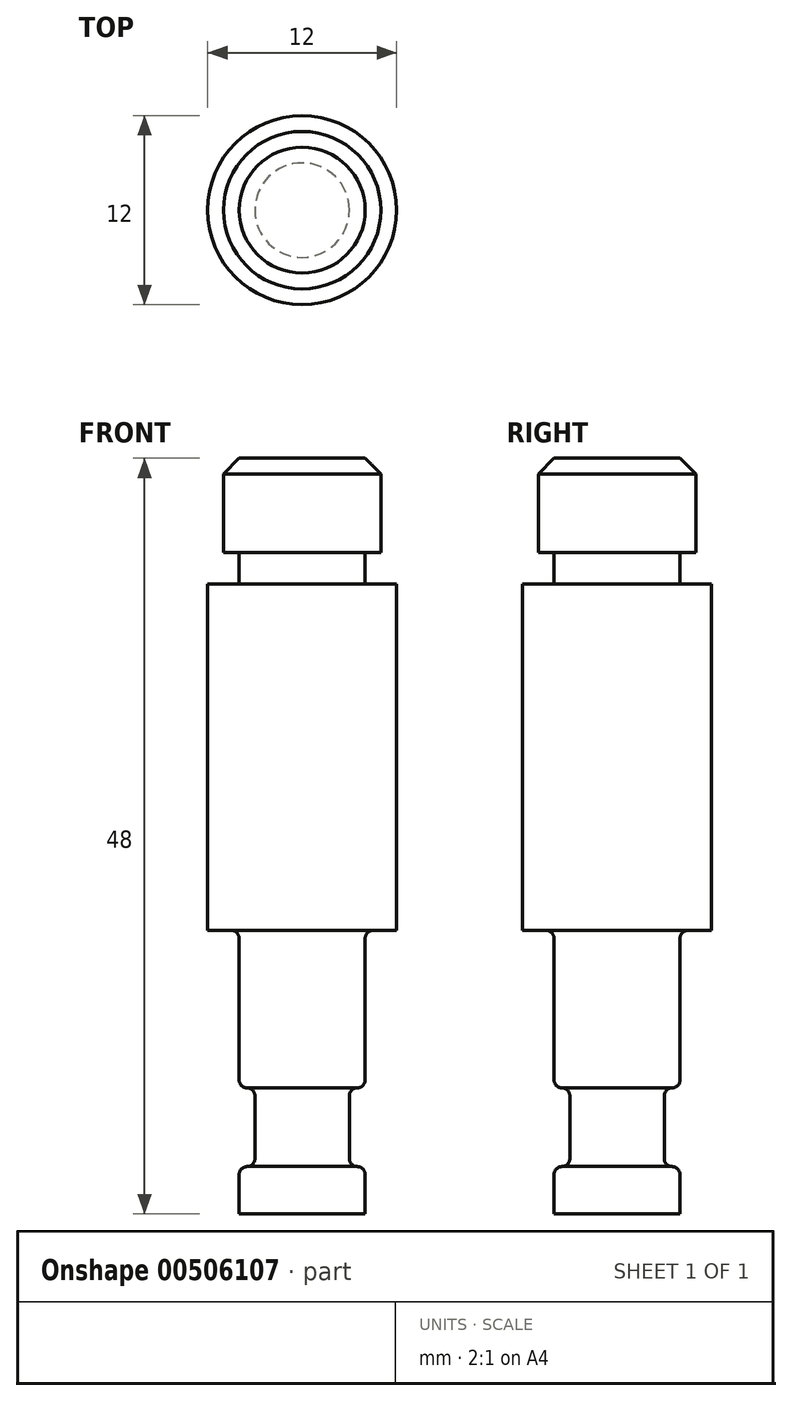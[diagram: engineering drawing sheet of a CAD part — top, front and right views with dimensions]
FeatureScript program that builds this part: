
annotation { "Feature Type Name" : "Feature", "Feature Type Description" : "" }
export const myFeature = defineFeature(function(context is Context, id is Id, definition is map)
    precondition{}
    {
        {
            var Q0;
            Q0=qCreatedBy(makeId("Top.planeOp"),FACE);
            var sketch = newSketch(context, id + "F0", { "sketchPlane" : qUnion([Q0])});
            skCircle(sketch, "E0", {"center": v(0, 0) * mm, "radius": 6 * mm});
            skSolve(sketch);
        }
        {
            var Q0;
            Q0=makeQuery(id+"F0.imprint","IMPRINT",FACE,{"disambiguationData":[TD([[makeQuery(id+"F0.imprint","IMPRINT",EDGE,{"derivedFrom":sQuery(id+"F0.wireOp",EDGE,"E0")}),1.0]])]});
            extrude(context, id + "F1", {"entities" : qUnion([Q0]), "oppositeDirection" : true, "depth" : 40 * mm});
        }
        {
            var Q0;
            Q0=makeQuery(id+"F1.opExtrude","CAP_FACE",FACE,{"disambiguationData":[OSD([sQuery(id+"F0.wireOp",EDGE,"E0")])],"isStart":true});
            var sketch = newSketch(context, id + "F2", { "sketchPlane" : qUnion([Q0])});
            skCircle(sketch, "E1", {"center": v(0, 0) * mm, "radius": 5 * mm});
            skSolve(sketch);
        }
        {
            var Q0;
            Q0 = qSketchRegion(id + "F2", true);
            extrude(context, id + "F3", {"entities" : qUnion([Q0]), "operationType" : NewBodyOperationType.ADD, "depth" : 8 * mm});
        }
        {
            var Q0;
            Q0=qCreatedBy(makeId("Right.planeOp"),FACE);
            var sketch = newSketch(context, id + "F4", { "sketchPlane" : qUnion([Q0])});
            skLineSegment(sketch, "E2", {"start": v(0, -52.59) * mm, "end": v(0, 0) * mm, "construction": true});
            skLineSegment(sketch, "E3", {"start": v(6, 0) * mm, "end": v(6, -40) * mm});
            skLineSegment(sketch, "E4", {"start": v(-6, -40) * mm, "end": v(-6, -22) * mm});
            skLineSegment(sketch, "E5", {"start": v(-4, -40) * mm, "end": v(-4, -37) * mm});
            skLineSegment(sketch, "E6", {"start": v(-4, -37) * mm, "end": v(-3, -37) * mm});
            skLineSegment(sketch, "E7", {"start": v(-3, -32) * mm, "end": v(-3, -37) * mm});
            skLineSegment(sketch, "E8", {"start": v(-4, -32) * mm, "end": v(-3, -32) * mm});
            skLineSegment(sketch, "E9", {"start": v(-4, -22) * mm, "end": v(-4, -32) * mm});
            skLineSegment(sketch, "E10", {"start": v(-6, -22) * mm, "end": v(-4, -22) * mm});
            skLineSegment(sketch, "E11.trimOffspring", {"start": v(-4, -40) * mm, "end": v(-6, -40) * mm});
            skPoint(sketch, "E12.0.0.start.orphan", {"position": v(6, -40) * mm});
            skSolve(sketch);
        }
        {
            var Q0;
            Q0 = qSketchRegion(id + "F4", true);
            var Q1;
            Q1=sQuery(id+"F4.wireOp",EDGE,"E2");
            revolve(context, id + "F5", {"operationType" : NewBodyOperationType.REMOVE, "entities" : qUnion([Q0]), "axis" : qUnion([Q1]), "revolveType" : RevolveType.FULL});
        }
        {
            var Q0;
            Q0=makeQuery(id+"F5.boolean.opBoolean","COPY",EDGE,{"derivedFrom":makeQuery(id+"F5.opRevolve","SWEPT_EDGE",EDGE,{"disambiguationData":[OSD([sQuery(id+"F4.wireOp",EDGE,"E5"),sQuery(id+"F4.wireOp",EDGE,"E11.trimOffspring")])]})});
            var Q1;
            Q1=makeQuery(id+"F5.boolean.opBoolean","COPY",EDGE,{"derivedFrom":makeQuery(id+"F5.opRevolve","SWEPT_EDGE",EDGE,{"disambiguationData":[OSD([sQuery(id+"F4.wireOp",EDGE,"E5"),sQuery(id+"F4.wireOp",EDGE,"E6")])]})});
            var Q2;
            Q2=makeQuery(id+"F5.boolean.opBoolean","COPY",EDGE,{"derivedFrom":makeQuery(id+"F5.opRevolve","SWEPT_EDGE",EDGE,{"disambiguationData":[OSD([sQuery(id+"F4.wireOp",EDGE,"E6"),sQuery(id+"F4.wireOp",EDGE,"E7")])]})});
            var Q3;
            Q3=makeQuery(id+"F5.boolean.opBoolean","COPY",EDGE,{"derivedFrom":makeQuery(id+"F5.opRevolve","SWEPT_EDGE",EDGE,{"disambiguationData":[OSD([sQuery(id+"F4.wireOp",EDGE,"E7"),sQuery(id+"F4.wireOp",EDGE,"E8")])]})});
            var Q4;
            Q4=makeQuery(id+"F5.boolean.opBoolean","COPY",EDGE,{"derivedFrom":makeQuery(id+"F5.opRevolve","SWEPT_EDGE",EDGE,{"disambiguationData":[OSD([sQuery(id+"F4.wireOp",EDGE,"E8"),sQuery(id+"F4.wireOp",EDGE,"E9")])]})});
            var Q5;
            Q5=makeQuery(id+"F5.boolean.opBoolean","COPY",EDGE,{"derivedFrom":makeQuery(id+"F5.opRevolve","SWEPT_EDGE",EDGE,{"disambiguationData":[OSD([sQuery(id+"F4.wireOp",EDGE,"E9"),sQuery(id+"F4.wireOp",EDGE,"E10")])]})});
            var Q6;
            Q6=makeQuery(id+"F5.boolean.opBoolean","COPY",EDGE,{"derivedFrom":makeQuery(id+"F5.opRevolve","SWEPT_EDGE",EDGE,{"disambiguationData":[OSD([sQuery(id+"F4.wireOp",EDGE,"E4"),sQuery(id+"F4.wireOp",EDGE,"E10")])]})});
            fillet(context, id + "F6", {"entities" : qUnion([Q0, Q1, Q2, Q3, Q4, Q5, Q6]), "radius" : 0.5 * mm, "tangentPropagation" : true, "allowEdgeOverflow" : false});
        }
        {
            var Q0;
            Q0=qCreatedBy(makeId("Right.planeOp"),FACE);
            var sketch = newSketch(context, id + "F7", { "sketchPlane" : qUnion([Q0])});
            skLineSegment(sketch, "E13", {"start": v(0, 0) * mm, "end": v(0, 22.3) * mm, "construction": true});
            skLineSegment(sketch, "E14", {"start": v(-5, 0) * mm, "end": v(-5, 2) * mm});
            skLineSegment(sketch, "E15", {"start": v(-5, 0) * mm, "end": v(-4, 0) * mm});
            skLineSegment(sketch, "E16", {"start": v(-4, 0) * mm, "end": v(-4, 2) * mm});
            skLineSegment(sketch, "E17", {"start": v(-5, 2) * mm, "end": v(-4, 2) * mm});
            skPoint(sketch, "E18.orphan", {"position": v(-5, 8) * mm});
            skSolve(sketch);
        }
        {
            var Q0;
            Q0 = qSketchRegion(id + "F7", true);
            var Q1;
            Q1=sQuery(id+"F7.wireOp",EDGE,"E13");
            revolve(context, id + "F8", {"operationType" : NewBodyOperationType.REMOVE, "entities" : qUnion([Q0]), "axis" : qUnion([Q1]), "revolveType" : RevolveType.FULL, "oppositeDirection" : true});
        }
        {
            var Q0;
            Q0=makeQuery(id+"F3.opExtrude","CAP_EDGE",EDGE,{"disambiguationData":[OSD([sQuery(id+"F2.wireOp",EDGE,"E1")])],"isStart":false});
            chamfer(context, id + "F9", {"entities" : qUnion([Q0]), "width" : 1 * mm, "tangentPropagation" : true});
        }
    });
